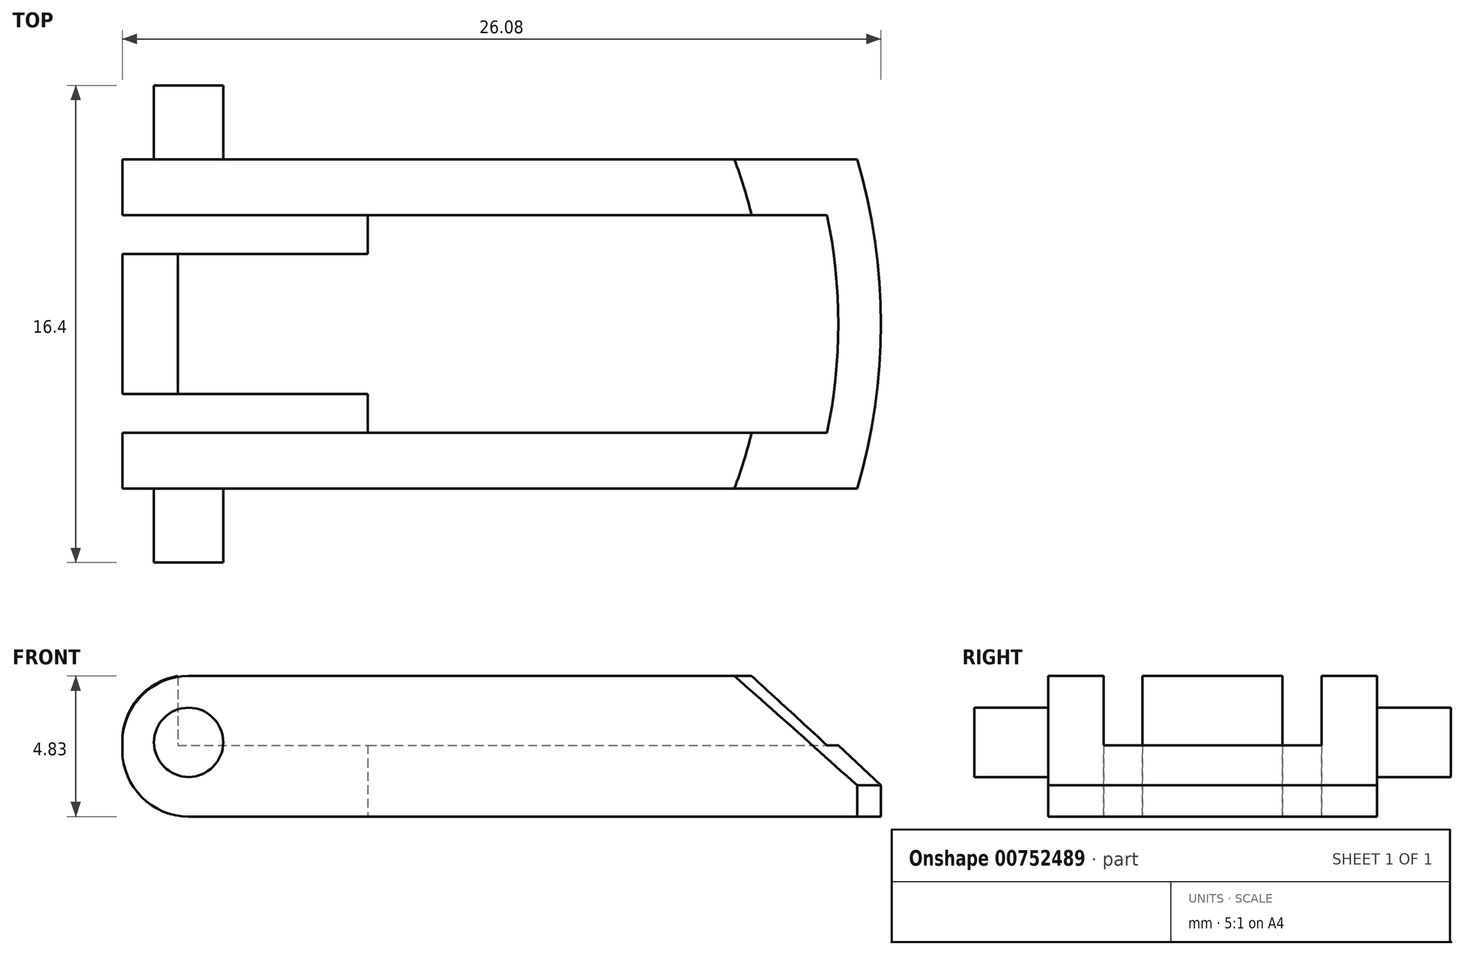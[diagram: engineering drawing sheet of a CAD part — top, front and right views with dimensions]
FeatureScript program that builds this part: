
annotation { "Feature Type Name" : "Feature", "Feature Type Description" : "" }
export const myFeature = defineFeature(function(context is Context, id is Id, definition is map)
    precondition{}
    {
        {
            var Q0;
            Q0=qCreatedBy(makeId("Top.planeOp"),FACE);
            var sketch = newSketch(context, id + "F0", { "sketchPlane" : qUnion([Q0])});
            skLineSegment(sketch, "E0.bottom", {"start": v(12.22, 5.65) * mm, "end": v(-13.04, 5.66) * mm});
            skLineSegment(sketch, "E0.top", {"start": v(12.22, -5.66) * mm, "end": v(-13.04, -5.65) * mm});
            skLineSegment(sketch, "E0.right", {"start": v(-13.04, 5.66) * mm, "end": v(-13.04, 3.74) * mm});
            skPoint(sketch, "E0.middle", {"position": v(0, 0) * mm});
            skLineSegment(sketch, "E1", {"start": v(-13.04, 3.75) * mm, "end": v(-4.6, 3.75) * mm});
            skLineSegment(sketch, "E2", {"start": v(-13.04, 2.4) * mm, "end": v(-4.6, 2.4) * mm});
            skLineSegment(sketch, "E3", {"start": v(-4.6, 3.74) * mm, "end": v(-4.6, 2.4) * mm});
            skLineSegment(sketch, "E4.trimOffspring", {"start": v(-13.04, 2.4) * mm, "end": v(-13.04, -2.4) * mm});
            skLineSegment(sketch, "E5.MirrorCS", {"start": v(-13.04, -3.74) * mm, "end": v(-4.6, -3.74) * mm});
            skLineSegment(sketch, "E6.MirrorCS", {"start": v(-4.6, -3.74) * mm, "end": v(-4.6, -2.4) * mm});
            skLineSegment(sketch, "E7.MirrorCS", {"start": v(-13.04, -2.4) * mm, "end": v(-4.6, -2.4) * mm});
            skLineSegment(sketch, "E8.trimOffspring", {"start": v(-13.04, -3.74) * mm, "end": v(-13.04, -5.65) * mm});
            skLineSegment(sketch, "E9", {"start": v(12.22, 5.65) * mm, "end": v(12.22, -5.66) * mm});
            skArc(sketch, "E10", {"start": v(12.22, -5.66) * mm, "mid": v(13.04, 0) * mm, "end": v(12.22, 5.65) * mm});
            skPoint(sketch, "E11.start.orphan", {"position": v(13.04, 0) * mm});
            skLineSegment(sketch, "E12", {"start": v(-9.5, 5.66) * mm, "end": v(-9.5, 8.14) * mm});
            skLineSegment(sketch, "E13", {"start": v(-9.5, 8.14) * mm, "end": v(-7.02, 8.14) * mm});
            skLineSegment(sketch, "E14", {"start": v(-7.02, 8.14) * mm, "end": v(-7.02, 5.66) * mm});
            skLineSegment(sketch, "E15.MirrorCS", {"start": v(-7.02, -8.14) * mm, "end": v(-7.02, -5.66) * mm});
            skLineSegment(sketch, "E16.MirrorCS", {"start": v(-9.5, -8.14) * mm, "end": v(-7.02, -8.14) * mm});
            skLineSegment(sketch, "E17.MirrorCS", {"start": v(-9.5, -5.66) * mm, "end": v(-9.5, -8.14) * mm});
            skSolve(sketch);
        }
        {
            var Q0;
            {var subQ0=sQuery(id+"F0.wireOp",EDGE,"E0.right");Q0=makeQuery(id+"F0.imprint","IMPRINT",FACE,{"disambiguationData":[TD([[makeQuery(id+"F0.imprint","IMPRINT",EDGE,{"derivedFrom":subQ0}),1.0]])]});}
            var Q1;
            Q1=makeQuery(id+"F0.imprint","IMPRINT",FACE,{"disambiguationData":[TD([[makeQuery(id+"F0.imprint","IMPRINT",EDGE,{"derivedFrom":sQuery(id+"F0.wireOp",EDGE,"E9")}),1.0]])]});
            extrude(context, id + "F1", {"entities" : qUnion([Q0, Q1]), "depth" : 2.45 * mm, "offsetDistance" : 25 * mm});
        }
        {
            var Q0;
            Q0=makeQuery(id+"F1.opExtrude","CAP_FACE",FACE,{"disambiguationData":[OSD([sQuery(id+"F0.wireOp",EDGE,"E0.bottom"),sQuery(id+"F0.wireOp",EDGE,"E0.top"),sQuery(id+"F0.wireOp",EDGE,"E0.right"),sQuery(id+"F0.wireOp",EDGE,"E1"),sQuery(id+"F0.wireOp",EDGE,"E2"),sQuery(id+"F0.wireOp",EDGE,"E3"),sQuery(id+"F0.wireOp",EDGE,"E4.trimOffspring"),sQuery(id+"F0.wireOp",EDGE,"E5.MirrorCS"),sQuery(id+"F0.wireOp",EDGE,"E6.MirrorCS"),sQuery(id+"F0.wireOp",EDGE,"E7.MirrorCS"),sQuery(id+"F0.wireOp",EDGE,"E8.trimOffspring"),sQuery(id+"F0.wireOp",EDGE,"E10")])],"isStart":false});
            var sketch = newSketch(context, id + "F2", { "sketchPlane" : qUnion([Q0])});
            skLineSegment(sketch, "E18.0", {"start": v(12.22, 5.65) * mm, "end": v(-13.04, 5.66) * mm});
            skLineSegment(sketch, "E18.1", {"start": v(12.22, -5.66) * mm, "end": v(-13.04, -5.65) * mm});
            skLineSegment(sketch, "E19.0", {"start": v(12.22, 5.7) * mm, "end": v(-13.04, 5.7) * mm});
            skLineSegment(sketch, "E20.0", {"start": v(12.68, 3.75) * mm, "end": v(-13.04, 3.75) * mm});
            skLineSegment(sketch, "E21.0", {"start": v(12.68, -3.74) * mm, "end": v(-13.04, -3.74) * mm});
            skLineSegment(sketch, "E22.0", {"start": v(-13.04, 2.4) * mm, "end": v(-13.04, -2.4) * mm});
            skLineSegment(sketch, "E23.0", {"start": v(-13.04, 5.66) * mm, "end": v(-13.04, 3.74) * mm});
            skLineSegment(sketch, "E24.0", {"start": v(-13.04, -3.74) * mm, "end": v(-13.04, -5.65) * mm});
            skArc(sketch, "E25.0", {"start": v(12.22, -5.66) * mm, "mid": v(13.04, 0) * mm, "end": v(12.22, 5.65) * mm});
            skLineSegment(sketch, "E26.0", {"start": v(-11.13, 5.66) * mm, "end": v(-11.13, 3.74) * mm});
            skLineSegment(sketch, "E27.0", {"start": v(-11.13, 2.4) * mm, "end": v(-11.13, -2.4) * mm});
            skLineSegment(sketch, "E28.0", {"start": v(-11.13, -3.74) * mm, "end": v(-11.13, -5.65) * mm});
            skSolve(sketch);
        }
        {
            var Q0;
            {var subQ6=sQuery(id+"F2.wireOp",EDGE,"E26.0");Q0=makeQuery(id+"F2.imprint","IMPRINT",FACE,{"disambiguationData":[TD([[makeQuery(id+"F2.imprint","IMPRINT",EDGE,{"derivedFrom":subQ6}),1.0]])]});}
            var Q1;
            {var subQ0=sQuery(id+"F2.wireOp",EDGE,"E23.0");Q1=makeQuery(id+"F2.imprint","IMPRINT",FACE,{"disambiguationData":[TD([[makeQuery(id+"F2.imprint","IMPRINT",EDGE,{"derivedFrom":subQ0}),1.0]])]});}
            var Q2;
            {var subQ0=sQuery(id+"F2.wireOp",EDGE,"E22.0");Q2=makeQuery(id+"F2.imprint","IMPRINT",FACE,{"disambiguationData":[TD([[makeQuery(id+"F2.imprint","IMPRINT",EDGE,{"derivedFrom":subQ0}),1.0]])]});}
            var Q3;
            {var subQ0=sQuery(id+"F2.wireOp",EDGE,"E24.0");Q3=makeQuery(id+"F2.imprint","IMPRINT",FACE,{"disambiguationData":[TD([[makeQuery(id+"F2.imprint","IMPRINT",EDGE,{"derivedFrom":subQ0}),1.0]])]});}
            var Q4;
            {var subQ2=sQuery(id+"F2.wireOp",EDGE,"E28.0");Q4=makeQuery(id+"F2.imprint","IMPRINT",FACE,{"disambiguationData":[TD([[makeQuery(id+"F2.imprint","IMPRINT",EDGE,{"derivedFrom":subQ2}),1.0]])]});}
            extrude(context, id + "F3", {"entities" : qUnion([Q0, Q1, Q2, Q3, Q4]), "operationType" : NewBodyOperationType.ADD, "depth" : 2.38 * mm, "offsetDistance" : 25 * mm});
        }
        {
            var Q0;
            Q0=makeQuery(id+"F3.opExtrude","CAP_EDGE",EDGE,{"disambiguationData":[OSD([sQuery(id+"F2.wireOp",EDGE,"E24.0")])],"isStart":false});
            var Q1;
            Q1=makeQuery(id+"F1.opExtrude","CAP_EDGE",EDGE,{"disambiguationData":[OSD([sQuery(id+"F0.wireOp",EDGE,"E8.trimOffspring")])],"isStart":true});
            var Q2;
            Q2=makeQuery(id+"F3.opExtrude","CAP_EDGE",EDGE,{"disambiguationData":[OSD([sQuery(id+"F2.wireOp",EDGE,"E23.0")])],"isStart":false});
            var Q3;
            Q3=makeQuery(id+"F1.opExtrude","CAP_EDGE",EDGE,{"disambiguationData":[OSD([sQuery(id+"F0.wireOp",EDGE,"E0.right")])],"isStart":true});
            var Q4;
            Q4=makeQuery(id+"F3.opExtrude","CAP_EDGE",EDGE,{"disambiguationData":[OSD([sQuery(id+"F2.wireOp",EDGE,"E22.0")])],"isStart":false});
            var Q5;
            Q5=makeQuery(id+"F1.opExtrude","CAP_EDGE",EDGE,{"disambiguationData":[OSD([sQuery(id+"F0.wireOp",EDGE,"E4.trimOffspring")])],"isStart":true});
            fillet(context, id + "F4", {"entities" : qUnion([Q0, Q1, Q2, Q3, Q4, Q5]), "radius" : 2.28 * mm, "tangentPropagation" : true, "allowEdgeOverflow" : false});
        }
        {
            var Q0;
            {var subQ0=sQuery(id+"F2.wireOp",EDGE,"E25.0");Q0=makeQuery(id+"F3.opExtrude","CAP_EDGE",EDGE,{"disambiguationData":[OSD([subQ0]),TDD([makeQuery(id+"F2.imprint","IMPRINT",EDGE,{"disambiguationData":[TD([[makeQuery(id+"F2.imprint","INTERSECT",VERTEX,{"derivedFrom":[sQuery(id+"F2.wireOp",EDGE,"E18.0"),subQ0]}),1.0]])],"derivedFrom":subQ0})])],"isStart":false});}
            chamfer(context, id + "F5", {"entities" : qUnion([Q0]), "chamferType" : ChamferType.TWO_OFFSETS, "width1" : 4 * mm, "oppositeDirection" : false, "width2" : 3.76 * mm, "tangentPropagation" : true});
        }
        {
            var Q0;
            Q0=makeQuery(id+"F3.boolean.opBoolean","MERGE",FACE,{"derivedFrom":[makeQuery(id+"F1.opExtrude","SWEPT_FACE",FACE,{"disambiguationData":[OSD([sQuery(id+"F0.wireOp",EDGE,"E0.top")])]}),makeQuery(id+"F3.opExtrude","SWEPT_FACE",FACE,{"disambiguationData":[OSD([sQuery(id+"F2.wireOp",EDGE,"E18.1")])]})]});
            var sketch = newSketch(context, id + "F6", { "sketchPlane" : qUnion([Q0])});
            skArc(sketch, "E29.0", {"start": v(-10.76, 4.83) * mm, "mid": v(-12.37, 4.16) * mm, "end": v(-13.04, 2.55) * mm});
            skCircle(sketch, "E30", {"center": v(-10.76, 2.55) * mm, "radius": 1.19 * mm});
            skSolve(sketch);
        }
        {
            var Q0;
            Q0=makeQuery(id+"F6.imprint","IMPRINT",FACE,{"disambiguationData":[TD([[makeQuery(id+"F6.imprint","IMPRINT",EDGE,{"derivedFrom":sQuery(id+"F6.wireOp",EDGE,"E30")}),1.0]])]});
            extrude(context, id + "F7", {"entities" : qUnion([Q0]), "depth" : 2.54 * mm, "offsetDistance" : 25 * mm});
        }
        {
            var Q0;
            Q0=makeQuery(id+"F7.opExtrude","SWEPT_BODY",BODY,{"disambiguationData":[OSD([sQuery(id+"F6.wireOp",EDGE,"E30")])]});
            var Q1;
            Q1=qCreatedBy(makeId("Front.planeOp"),FACE);
            mirror(context, id + "F8", {"operationType" : NewBodyOperationType.ADD, "entities" : qUnion([Q0]), "mirrorPlane" : qUnion([Q1])});
        }
    });
